# Revit family: Mailboxes_4C-Salsbury_Industries-Rear_Load-10_Door_High_Units
name_source: partatom
category: Specialty Equipment
revit_build: Autodesk Revit 2016 (Build: 20190507_1515(x64)
units: mm (PartAtom-declared; Revit-internal decimal feet)

## family parameters
Cut with Voids When Loaded = No
Host = Face
OmniClass Number = 23.40.90.14.11
OmniClass Title = Mail Boxes
Part Type = Normal
Room Calculation Point = No
Round Connector Dimension = Use Diameter
Shared = No

## types (9) — shared parameters
Assembly Code = C1030910
Assembly Description = Mailboxes
Back Enclosure Material = Aluminum Alloy - Salsbury Finish - Clear (No finish)
Bottom Back Plate = No
Center Divider Offset = 14.381"
Center Extrusion Offset = 0.000"
Decals = Polycarbonate Film - Salsbury Finish - White
Depth = 16.450"
Door Depth = 0.190"
Door Slot R3 = 3700 Series 4C Door Configurations : Empty
Height = 37.875"
Lock Material = Stainless Steel - Salsbury Finish -  Polished
Manufacturer = Salsbury Industries
MasterFormat Number = 10 55 00
MasterFormat Title = Postal Specialties
OmniClass 23 Number = 23.40.90.14.11
OmniClass 23 Title = Mail Boxes
Rough Opening - Height = 36.625"
Top Back Plate = No
URL = www.mailboxes.com
Version = 5.0 (01/01/21)

## per-type parameters (varying)
| type | Description | Door Slot L1 | Door Slot L10 | Door Slot L2 | Door Slot L3 | Door Slot L4 | Door Slot L5 | Door Slot L6 | Door Slot R1 | Door Slot R10 | Door Slot R2 | Door Slot R3.5 | Door Slot R4 | Door Slot R4.5 | Door Slot R5 | Door Slot R5.5 | Double Wide Hidden Components | Left Inside Wall | Right Inside Wall | Rough Opening - Width | Type Comments | Vertical Center Divider | Visible Latches | Width |
| 3710D-10 RL | 10 Door High Unit: 10 MB1, 1 PL4, 1 PL4.5, OM1.5 | 3700 Series 4C Door Configurations : MB1 Door | 3700 Series 4C Parcel Configurations : PL4 w/ Divider | 3700 Series 4C Door Configurations : MB1 Door w/ Divider | 3700 Series 4C Door Configurations : MB1 Door w/ Divider | 3700 Series 4C Door Configurations : MB1 Door w/ Divider | 3700 Series 4C Door Configurations : MB1 Door w/ Divider | 3700 Series 4C Door Configurations : MB1 Door w/ Divider | 3700 Series 4C Door Configurations : MB1 Door | 3700 Series 4C Parcel Configurations : PL4.5 w/ Divider | 3700 Series 4C Door Configurations : MB1 Door w/ Divider | 3700 Series 4C OM1.5 Configuration : OM1.5-RL | 3700 Series 4C Door Configurations : Empty | 3700 Series 4C Door Configurations : MB1 Door w/ Divider | 3700 Series 4C Door Configurations : Empty | 3700 Series 4C Door Configurations : MB1 Door w/ Divider | Yes | Yes | Yes | 29.875" | 4C Standard Horizontal Mailbox - Rear Loading | Yes | Yes | 31.097" |
| 3710S-04 RL | 10 Door High Unit: 4 MB1, 1 PL4.5, OM1.5 | 3700 Series 4C Door Configurations : Empty | 3700 Series 4C Door Configurations : Empty | 3700 Series 4C Door Configurations : Empty | 3700 Series 4C Door Configurations : Empty | 3700 Series 4C Door Configurations : Empty | 3700 Series 4C Door Configurations : Empty | 3700 Series 4C Door Configurations : Empty | 3700 Series 4C Door Configurations : MB1 Door | 3700 Series 4C Parcel Configurations : PL4.5 w/ Divider | 3700 Series 4C Door Configurations : MB1 Door w/ Divider | 3700 Series 4C OM1.5 Configuration : OM1.5-RL | 3700 Series 4C Door Configurations : Empty | 3700 Series 4C Door Configurations : MB1 Door w/ Divider | 3700 Series 4C Door Configurations : Empty | 3700 Series 4C Door Configurations : MB1 Door w/ Divider | No | No | No | 15.750" | 4C Standard Horizontal Mailbox - Rear Loading | No | No | 16.966" |
| 3710D-09 RL | 10 Door High Unit: 9 MB1, 1 PL4.5, 1 PL5, OM1.5 | 3700 Series 4C Door Configurations : MB1 Door | 3700 Series 4C Parcel Configurations : PL5 w/ Divider | 3700 Series 4C Door Configurations : MB1 Door w/ Divider | 3700 Series 4C Door Configurations : MB1 Door w/ Divider | 3700 Series 4C Door Configurations : MB1 Door w/ Divider | 3700 Series 4C Door Configurations : MB1 Door w/ Divider | 3700 Series 4C Door Configurations : Empty | 3700 Series 4C Door Configurations : MB1 Door | 3700 Series 4C Parcel Configurations : PL4.5 w/ Divider | 3700 Series 4C Door Configurations : MB1 Door w/ Divider | 3700 Series 4C OM1.5 Configuration : OM1.5-RL | 3700 Series 4C Door Configurations : Empty | 3700 Series 4C Door Configurations : MB1 Door w/ Divider | 3700 Series 4C Door Configurations : Empty | 3700 Series 4C Door Configurations : MB1 Door w/ Divider | Yes | Yes | Yes | 29.875" | 4C Standard Horizontal Mailbox - Rear Loading | Yes | Yes | 31.097" |
| 3710D-06 RL | 10 Door High Unit: 6 MB1, 2 PL6, OM2 | 3700 Series 4C Door Configurations : MB1 Door | 3700 Series 4C Parcel Configurations : PL6 w/ Divider | 3700 Series 4C Door Configurations : MB1 Door w/ Divider | 3700 Series 4C Door Configurations : MB1 Door w/ Divider | 3700 Series 4C Door Configurations : MB1 Door w/ Divider | 3700 Series 4C Door Configurations : Empty | 3700 Series 4C Door Configurations : Empty | 3700 Series 4C Door Configurations : MB1 Door | 3700 Series 4C Parcel Configurations : PL6 w/ Divider | 3700 Series 4C Door Configurations : MB1 Door w/ Divider | 3700 Series 4C Door Configurations : Empty | 3700 Series 4C OM2 Configuration : OM2-RL | 3700 Series 4C Door Configurations : Empty | 3700 Series 4C Door Configurations : Empty | 3700 Series 4C Door Configurations : Empty | Yes | Yes | Yes | 29.875" | 4C Standard Horizontal Mailbox - Rear Loading | Yes | Yes | 31.097" |
| 3710D-4P RL | 10 Door High Unit:  4 PL5 | 3700 Series 4C Door Configurations : Empty | 3700 Series 4C Parcel Configurations : PL5 w/ Divider | 3700 Series 4C Door Configurations : Empty | 3700 Series 4C Door Configurations : Empty | 3700 Series 4C Door Configurations : Empty | 3700 Series 4C Parcel Configurations : PL5 | 3700 Series 4C Door Configurations : Empty | 3700 Series 4C Door Configurations : Empty | 3700 Series 4C Parcel Configurations : PL5 w/ Divider | 3700 Series 4C Door Configurations : Empty | 3700 Series 4C Door Configurations : Empty | 3700 Series 4C Door Configurations : Empty | 3700 Series 4C Door Configurations : Empty | 3700 Series 4C Parcel Configurations : PL5 | 3700 Series 4C Door Configurations : Empty | Yes | Yes | Yes | 29.875" | 4C Standard Horizontal Mailbox - Rear Loading | Yes | Yes | 31.097" |
| 3710S-03 RL | 10 Door High Unit: 3 MB1, 1 PL5, OM2 | 3700 Series 4C Door Configurations : Empty | 3700 Series 4C Door Configurations : Empty | 3700 Series 4C Door Configurations : Empty | 3700 Series 4C Door Configurations : Empty | 3700 Series 4C Door Configurations : Empty | 3700 Series 4C Door Configurations : Empty | 3700 Series 4C Door Configurations : Empty | 3700 Series 4C Door Configurations : MB1 Door | 3700 Series 4C Parcel Configurations : PL5 w/ Divider | 3700 Series 4C Door Configurations : MB1 Door w/ Divider | 3700 Series 4C Door Configurations : Empty | 3700 Series 4C OM2 Configuration : OM2-RL | 3700 Series 4C Door Configurations : Empty | 3700 Series 4C Door Configurations : MB1 Door w/ Divider | 3700 Series 4C Door Configurations : Empty | No | No | No | 15.750" | 4C Standard Horizontal Mailbox - Rear Loading | No | No | 16.966" |
| 3710S-2P RL | 10 Door High Unit:  2 PL5 | 3700 Series 4C Door Configurations : Empty | 3700 Series 4C Door Configurations : Empty | 3700 Series 4C Door Configurations : Empty | 3700 Series 4C Door Configurations : Empty | 3700 Series 4C Door Configurations : Empty | 3700 Series 4C Door Configurations : Empty | 3700 Series 4C Door Configurations : Empty | 3700 Series 4C Door Configurations : Empty | 3700 Series 4C Parcel Configurations : PL5 w/ Divider | 3700 Series 4C Door Configurations : Empty | 3700 Series 4C Door Configurations : Empty | 3700 Series 4C Door Configurations : Empty | 3700 Series 4C Door Configurations : Empty | 3700 Series 4C Parcel Configurations : PL5 | 3700 Series 4C Door Configurations : Empty | No | No | No | 15.750" | 4C Standard Horizontal Mailbox - Rear Loading | No | No | 16.966" |
| 3710S-1B RL | 10 Door High Unit:  1 Receptacle | 3700 Series 4C Door Configurations : Empty | 3700 Series 4C Door Configurations : Empty | 3700 Series 4C Door Configurations : Empty | 3700 Series 4C Door Configurations : Empty | 3700 Series 4C Door Configurations : Empty | 3700 Series 4C Door Configurations : Empty | 3700 Series 4C Door Configurations : Empty | 3700 Series 4C Door Configurations : Empty | 4C-10 Door High Receptacle | 3700 Series 4C Door Configurations : Empty | 3700 Series 4C Door Configurations : Empty | 3700 Series 4C Door Configurations : Empty | 3700 Series 4C Door Configurations : Empty | 3700 Series 4C Door Configurations : Empty | 3700 Series 4C Door Configurations : Empty | No | No | No | 15.750" | 4C Standard Horizontal Receptacle Bin - Rear Loading | No | No | 16.966" |
| 3710S-1C RL | 10 Door High Unit:  1 Collection Box | 3700 Series 4C Door Configurations : Empty | 3700 Series 4C Door Configurations : Empty | 3700 Series 4C Door Configurations : Empty | 3700 Series 4C Door Configurations : Empty | 3700 Series 4C Door Configurations : Empty | 3700 Series 4C Door Configurations : Empty | 3700 Series 4C Door Configurations : Empty | 3700 Series 4C Door Configurations : Empty | 4C-10 Door High Collection Box | 3700 Series 4C Door Configurations : Empty | 3700 Series 4C Door Configurations : Empty | 3700 Series 4C Door Configurations : Empty | 3700 Series 4C Door Configurations : Empty | 3700 Series 4C Door Configurations : Empty | 3700 Series 4C Door Configurations : Empty | No | No | No | 15.750" | 4C Standard Horizontal Collection Box - Rear Loading | No | No | 16.966" |

note: column(s) folded — value = type name in every type: Model

## geometry (parser evidence)
native form markers: Extrusion x2, Sweep x44
no freeform markers — native parametric forms only
